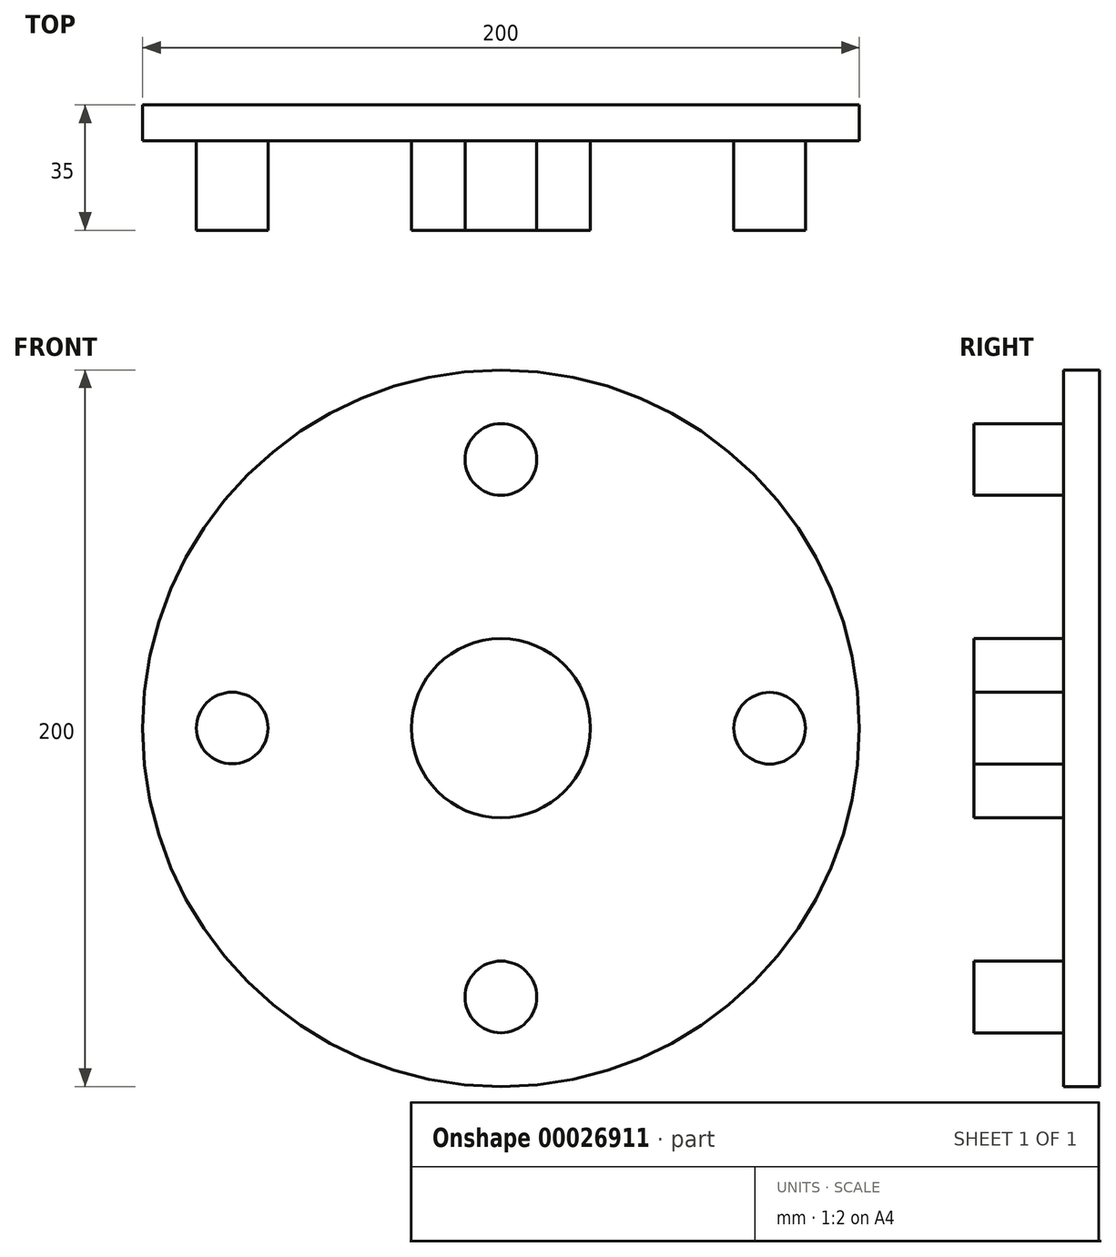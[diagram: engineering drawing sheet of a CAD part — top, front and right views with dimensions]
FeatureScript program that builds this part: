
annotation { "Feature Type Name" : "Feature", "Feature Type Description" : "" }
export const myFeature = defineFeature(function(context is Context, id is Id, definition is map)
    precondition{}
    {
        {
            var Q0;
            Q0=qCreatedBy(makeId("Front.planeOp"),FACE);
            var sketch = newSketch(context, id + "F0", { "sketchPlane" : qUnion([Q0])});
            skCircle(sketch, "E0", {"center": v(0, 0) * mm, "radius": 100 * mm});
            skSolve(sketch);
        }
        {
            var Q0;
            Q0=qSketchRegion(id+"F0",true);
            extrude(context, id + "F1", {"entities" : qUnion([Q0]), "depth" : 10 * mm});
        }
        {
            var Q0;
            Q0=makeQuery(id+"F1.opExtrude","CAP_FACE",FACE,{"disambiguationData":[OSD([sQuery(id+"F0.wireOp",EDGE,"E0")])],"isStart":false});
            var sketch = newSketch(context, id + "F2", { "sketchPlane" : qUnion([Q0])});
            skCircle(sketch, "E1", {"center": v(0, 75) * mm, "radius": 10 * mm});
            skCircle(sketch, "E2", {"center": v(75, 0) * mm, "radius": 10 * mm});
            skCircle(sketch, "E3", {"center": v(0, -75) * mm, "radius": 10 * mm});
            skCircle(sketch, "E4", {"center": v(-75, 0.06) * mm, "radius": 10 * mm});
            skSolve(sketch);
        }
        {
            var Q0;
            Q0=makeQuery(id+"F2.imprint","IMPRINT",FACE,{"disambiguationData":[TD([[makeQuery(id+"F2.imprint","IMPRINT",EDGE,{"derivedFrom":sQuery(id+"F2.wireOp",EDGE,"E1")}),1.0]])]});
            var Q1;
            Q1=makeQuery(id+"F2.imprint","IMPRINT",FACE,{"disambiguationData":[TD([[makeQuery(id+"F2.imprint","IMPRINT",EDGE,{"derivedFrom":sQuery(id+"F2.wireOp",EDGE,"E4")}),1.0]])]});
            var Q2;
            Q2=makeQuery(id+"F2.imprint","IMPRINT",FACE,{"disambiguationData":[TD([[makeQuery(id+"F2.imprint","IMPRINT",EDGE,{"derivedFrom":sQuery(id+"F2.wireOp",EDGE,"E2")}),1.0]])]});
            var Q3;
            Q3=makeQuery(id+"F2.imprint","IMPRINT",FACE,{"disambiguationData":[TD([[makeQuery(id+"F2.imprint","IMPRINT",EDGE,{"derivedFrom":sQuery(id+"F2.wireOp",EDGE,"E3")}),1.0]])]});
            var Q4;
            Q4=sQuery(id+"F2.wireOp",EDGE,"E1");
            extrude(context, id + "F3", {"entities" : qUnion([Q0, Q1, Q2, Q3]), "operationType" : NewBodyOperationType.ADD, "surfaceEntities" : qUnion([Q4]), "depth" : 25 * mm});
        }
        {
            var Q0;
            Q0=makeQuery(id+"F1.opExtrude","CAP_FACE",FACE,{"disambiguationData":[OSD([sQuery(id+"F0.wireOp",EDGE,"E0")])],"isStart":false});
            var sketch = newSketch(context, id + "F4", { "sketchPlane" : qUnion([Q0])});
            skCircle(sketch, "E5", {"center": v(0, 0) * mm, "radius": 25 * mm});
            skSolve(sketch);
        }
        {
            var Q0;
            Q0 = qSketchRegion(id + "F4", true);
            extrude(context, id + "F5", {"entities" : qUnion([Q0]), "operationType" : NewBodyOperationType.ADD, "depth" : 25 * mm});
        }
    });
